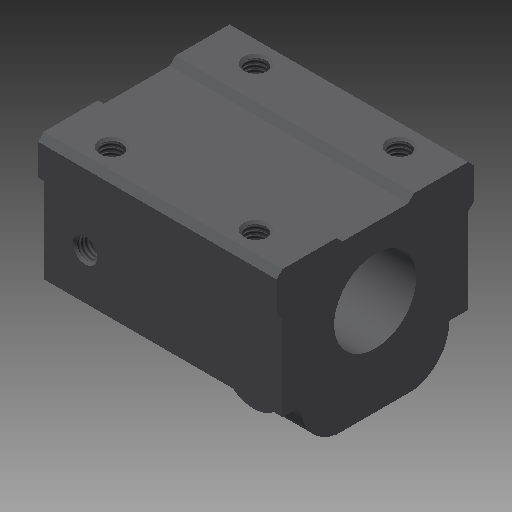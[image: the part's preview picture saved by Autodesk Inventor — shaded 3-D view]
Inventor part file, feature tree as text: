
AUTODESK INVENTOR PART (.ipt)
format: ipt  version: 2018 (Build 220112000, 112)  size: 225,792 bytes
history: native  units: mm
features: sketch x9, other x7, extrude x5, revolve x2, hole x2, pattern_linear x1
ambient origin geometry x8: Origin, YZ Plane, XZ Plane, XY Plane, X Axis, Y Axis, Z Axis, Center Point
bodies: Solid1 (feature_tree)
feature tree (26):
  extrude  "Extrusion1"  Depth=58.0mm TaperAngle=0.0deg
  extrude  "Extrusion2"  TaperAngle=360.0deg  [1 undecoded]
  extrude  "Extrusion3"  Depth=0.8mm TaperAngle=0.0deg
  revolve  "Revolution1"  [1 undecoded]
  revolve  "Revolution2"  [1 undecoded]
  extrude  "Extrusion4"  [1 undecoded]
  extrude  "Extrusion5"  [1 undecoded]
  hole  "Hole1"  [1 undecoded]
  hole  "Hole2"  [1 undecoded]
  pattern_linear  "Rectangular Pattern1"  [2 undecoded]
  other  "bnt_nut_1_XY"
  other  "bnt_nut_1_YZ"
  other  "bnt_nut_1_ZX"
  other  "bnt_nut_1_X"
  other  "bnt_nut_1_Y"
  other  "bnt_nut_1_Z"
  other  "bnt_nut_1_Center"
  sketch  "Sketch_1"  dims[d0=58.0mm d1=0.0mm d2=58.0mm d3=0.0mm]
  sketch  "Sketch_2"  dims[d4=4.6mm d5=0.0mm d6=360.0deg]
  sketch  "Sketch_3"  dims[d7=360.0deg d8=0.8mm d9=0.0mm]
  sketch  "Sketch_4"  dims[d10=0.8mm d11=0.0mm]
  sketch  "Sketch_5"  dims[d12=4.917mm d13=10.5415mm d14=6.0mm d15=2.0mm d16=90.0deg d17=14.140584mm d18=120.0deg]
  sketch  "Sketch_6"  dims[d19=4.917mm d20=10.5415mm d21=6.0mm d22=2.0mm d23=90.0deg d24=13.140584mm d25=120.0deg d26=20.0mm d28=35.0mm d29=20.0mm d31=35.0mm]
  sketch  "Sketch_7"  dims[d32=0.0mm]
  sketch  "Sketch8"
  sketch  "Sketch9"
note: 9 required parameter values undecoded (feature->parameter linkage not recoverable at this tier; creation-order binding heuristic only, values carry confidence <= 0.55)